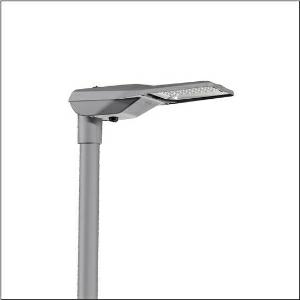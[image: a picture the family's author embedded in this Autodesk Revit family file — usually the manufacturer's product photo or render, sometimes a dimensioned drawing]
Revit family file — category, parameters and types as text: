
# Revit family: streetlight_sl_21_mini___st1_0ab_5xe2m33t08hb_c013
name_source: partatom
category: Lighting Fixtures
units: mm (PartAtom-declared; Revit-internal decimal feet)

## family parameters
Cut with Voids When Loaded = No
Host = Face
Light Source = No
Part Type = Normal
Room Calculation Point = No
Round Connector Dimension = Use Diameter
Shared = No

## types (1)
- --- (1 x LED, 7960 lm, 66 W, 3000K)
    Apparent Load = 66 VA
    CIE Flux Codes = 38 73 97 100 100
    Color Rendering = 70
    Color Temperature = 3000K
    Default Elevation = 1800 mm
    Description = Streetlight SL 21 mini, mast luminaire, primary light control with lens, of PMMA, primary optical cover: cover, of toughened safety glass, transparent, light distribution: ST1.0aB, light emission: direct distribution, primary light characteristic: asymmetric, installation type: side-entry, post-top, LED, High Power LED, rated luminous flux: 7.960lm, luminous efficacy: 121lm/W, light colour: 730, colour temperature: 3000K, control gear: D4i, control: flexible luminous flux parameterisation, time-dependent luminous flux control, constant luminous flux control, overheat protection, pre-setting: logarithmic dimming characteristic, mains connection: 220..240V, AC, 50/60Hz, start of lifetime: 66W, end of service life: 69W, reduction: 30W, luminaire housing, of diecast aluminium, powder-coated, SITECO metallic grey (DB 702S), corrosivity category C5 high according to DIN EN ISO 12944, please order mast flange separately, inclination adjustable: 0°, 5°, 10°, 15°, sealing non-destructively replaceable, multi-level sealing system, length: 628mm, width: 235mm, height: 110mm, mast flange for spigot size: 42mm (side-entry): 5XC10008XM4, 60/48mm (side-entry/post-top): 5XC10108XM2, 76/60mm (side-entry/post-top): 5XC10108XM1, mounting height: 4..8m, Smart Interface below and above, protection rating (complete): IP66, insulation class (complete): insulation class II (safety insulation), certification: CE, ENEC, ENEC+, VDE, impact resistance: IK10, permissible operating ambient temperature for outdoor applications: -40..+50°C, standard-compliant lighting for roads and squares, packaging unit: 1 piece

Light Distribution: ST1.0aB
    Height = 110 mm
    Lamp = 1 x LED
    Lamp Light Flux = 7960 lm
    Lamp Power = 66 W
    Lamp count = 1
    Length = 625 mm
    Luminous efficacy = 121 lm/W
    Manufacturer = Siteco
    ModVariant = No
    Model = 5XE2M33T08HB
    Number of Poles = 1
    OnlyDefault = Yes
    Power Factor = 1
    Product Name = Streetlight SL 21 mini | ST1.0aB
    Product group = mast luminaire | pylon top
    ProductGroupID = 6100
    Protection Class = Protection class II
    Protection Degree = IP 66
    RLX_Detail_Level = 1
    RLX_Emergency_Light_Flux = 0 lm
    RLX_Emergency_Type = 0
    RLX_Emergency_Type_DB = No
    RlxData = <blob elided: 26229 chars, md5=ba5e5d4a>
    Socket = socket
    Standby Power = 0 W
    System Light Flux = 7960 lm
    System Power = 66 W
    Type Comments = factory setting: luminous flux: 100 % | dim-lin: 254 | 670 mA
    Type Image = l_1003514.jpg
    URL = http://relux.com
    VarID = @adj_179971
    Voltage = 0 V
    Weight = 0.00 kg
    Width = 234 mm

## geometry (parser evidence)
native form markers: Blend x4, Sweep x11
no freeform markers — native parametric forms only
